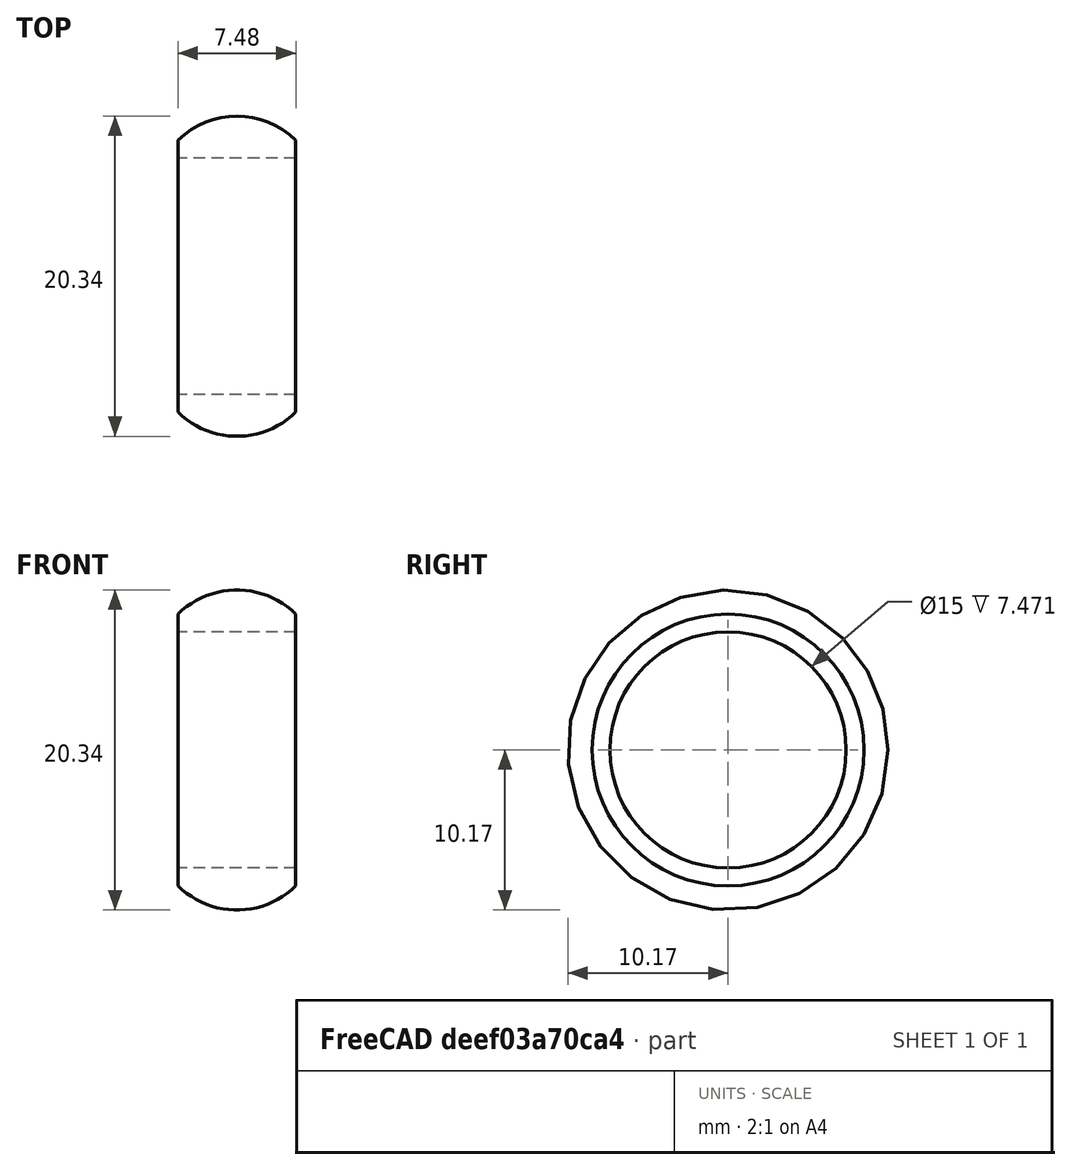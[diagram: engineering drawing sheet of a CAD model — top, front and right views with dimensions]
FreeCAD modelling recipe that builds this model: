
FCSTD DOCUMENT  (FreeCAD 0.16R6705 (Git))
Label: Anello_ele
License: All rights reserved
LicenseURL: http://it.wikipedia.org/wiki/<copyright redacted>
objects: Sketcher::SketchObject×1, PartDesign::Revolution×1
note: 3 computed .brp shape members not serialized (recipe doc carries the construction recipe); baked Part::Feature solids carry a one-line shape summary decoded from their .brp

FEATURE [Sketcher::SketchObject] Sketch
  sketch-geometry (4):
    g0: ArcOfCircle CenterX=0 CenterY=4.84318 CenterZ=0 NormalX=0 NormalY=0 NormalZ=1 Radius=5.32229 StartAngle=0.792778 EndAngle=2.34881
    g1: LineSegment StartX=-3.73555 StartY=8.63427 StartZ=0 EndX=-3.73555 EndY=7.5 EndZ=0
    g2: LineSegment StartX=3.73555 StartY=8.63427 StartZ=0 EndX=3.73555 EndY=7.5 EndZ=0
    g3: LineSegment StartX=3.73555 StartY=7.5 StartZ=0 EndX=-3.73555 EndY=7.5 EndZ=0
  constraints (9):
    c: Symmetric(g0,g0,g-2)
    c: Coincident(g1,g3)
    c: Coincident(g3,g2)
    c: Coincident(g0,g2)
    c: Coincident(g0,g1)
    c: Vertical(g1)
    c: Vertical(g2)
    c: Equal(g1,g2)
    c: DistanceY(g-1,g1) = 7.5
FEATURE [PartDesign::Revolution] Revolution
  Angle = 360
  Axis = (1,0,0)
  Base = (0,0,0)
  ReferenceAxis = -> Sketch [H_Axis]
  Sketch = -> Sketch
